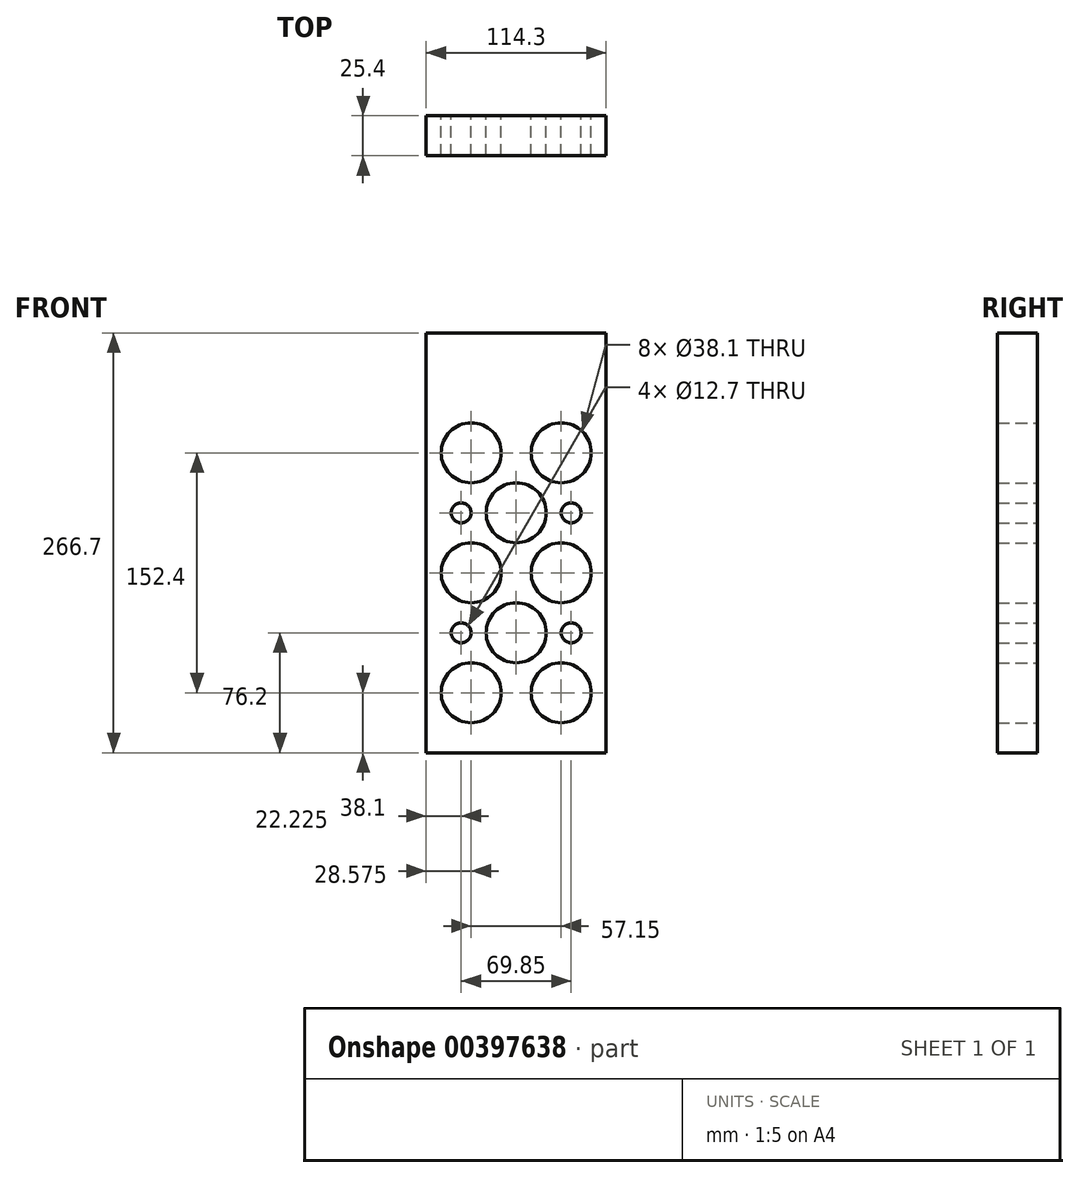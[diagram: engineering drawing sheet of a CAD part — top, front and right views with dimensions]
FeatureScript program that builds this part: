
annotation { "Feature Type Name" : "Feature", "Feature Type Description" : "" }
export const myFeature = defineFeature(function(context is Context, id is Id, definition is map)
    precondition{}
    {
        {
            var Q0;
            Q0=qCreatedBy(makeId("Front.planeOp"),FACE);
            var sketch = newSketch(context, id + "F0", { "sketchPlane" : qUnion([Q0])});
            skLineSegment(sketch, "E0.bottom", {"start": v(0, 0) * mm, "end": v(-114.3, 0) * mm});
            skLineSegment(sketch, "E0.top", {"start": v(0, 266.7) * mm, "end": v(-114.3, 266.7) * mm});
            skLineSegment(sketch, "E0.left", {"start": v(0, 0) * mm, "end": v(0, 266.7) * mm});
            skLineSegment(sketch, "E0.right", {"start": v(-114.3, 0) * mm, "end": v(-114.3, 266.7) * mm});
            skSolve(sketch);
        }
        {
            var Q0;
            Q0=makeQuery(id+"F0.imprint","IMPRINT",FACE,{"disambiguationData":[TD([[makeQuery(id+"F0.imprint","IMPRINT",EDGE,{"derivedFrom":sQuery(id+"F0.wireOp",EDGE,"E0.bottom")}),-1.0]])]});
            var sketch = newSketch(context, id + "F1", { "sketchPlane" : qUnion([Q0])});
            skLineSegment(sketch, "E1", {"start": v(0, 0) * mm, "end": v(-57.15, 0) * mm});
            skLineSegment(sketch, "E2", {"start": v(0, 0) * mm, "end": v(-28.58, 0) * mm});
            skLineSegment(sketch, "E3", {"start": v(0, 0) * mm, "end": v(-85.73, 0) * mm});
            skLineSegment(sketch, "E4", {"start": v(0, 0) * mm, "end": v(-114.3, 0) * mm});
            skLineSegment(sketch, "E5", {"start": v(-28.58, 0) * mm, "end": v(-28.58, 38.1) * mm, "construction": true});
            skLineSegment(sketch, "E6", {"start": v(-85.73, 0) * mm, "end": v(-85.73, 38.1) * mm, "construction": true});
            skCircle(sketch, "E7", {"center": v(-85.73, 38.1) * mm, "radius": 19.05 * mm});
            skCircle(sketch, "E8", {"center": v(-28.58, 38.1) * mm, "radius": 19.05 * mm});
            skLineSegment(sketch, "E9", {"start": v(-57.15, 0) * mm, "end": v(-57.15, 76.2) * mm, "construction": true});
            skCircle(sketch, "E10", {"center": v(-57.15, 76.2) * mm, "radius": 19.05 * mm});
            skCircle(sketch, "E11.0.1.0", {"center": v(-57.15, 152.4) * mm, "radius": 19.05 * mm});
            skCircle(sketch, "E11.0.1.1", {"center": v(-28.58, 114.3) * mm, "radius": 19.05 * mm});
            skCircle(sketch, "E11.0.1.2", {"center": v(-85.73, 114.3) * mm, "radius": 19.05 * mm});
            skCircle(sketch, "E11.0.2.1", {"center": v(-28.58, 190.5) * mm, "radius": 19.05 * mm});
            skCircle(sketch, "E11.0.2.2", {"center": v(-85.73, 190.5) * mm, "radius": 19.05 * mm});
            skLineSegment(sketch, "E11.direction1", {"start": v(-84.46, 31.75) * mm, "end": v(-59.06, 31.75) * mm, "construction": true});
            skLineSegment(sketch, "E11.direction2", {"start": v(-84.46, 31.75) * mm, "end": v(-84.46, 107.95) * mm, "construction": true});
            skSolve(sketch);
        }
        {
            var Q0;
            Q0=makeQuery(id+"F0.imprint","IMPRINT",FACE,{"disambiguationData":[TD([[makeQuery(id+"F0.imprint","IMPRINT",EDGE,{"derivedFrom":sQuery(id+"F0.wireOp",EDGE,"E0.bottom")}),-1.0]])]});
            var sketch = newSketch(context, id + "F2", { "sketchPlane" : qUnion([Q0])});
            skLineSegment(sketch, "E12", {"start": v(0, 0) * mm, "end": v(-22.23, 0) * mm});
            skLineSegment(sketch, "E13", {"start": v(0, 0) * mm, "end": v(-92.08, 0) * mm});
            skPoint(sketch, "E13.endSnap0", {"position": v(-11.11, 0) * mm});
            skLineSegment(sketch, "E14", {"start": v(-22.23, 0) * mm, "end": v(-22.23, 76.2) * mm});
            skLineSegment(sketch, "E15", {"start": v(-92.08, 0) * mm, "end": v(-92.08, 76.2) * mm});
            skCircle(sketch, "E16", {"center": v(-22.23, 76.2) * mm, "radius": 6.35 * mm});
            skCircle(sketch, "E17", {"center": v(-92.08, 76.2) * mm, "radius": 6.35 * mm});
            skCircle(sketch, "E18.0.1.0", {"center": v(-92.08, 152.4) * mm, "radius": 6.35 * mm});
            skCircle(sketch, "E18.0.1.1", {"center": v(-22.23, 152.4) * mm, "radius": 6.35 * mm});
            skLineSegment(sketch, "E18.direction1", {"start": v(-92.08, 76.2) * mm, "end": v(-66.68, 76.2) * mm, "construction": true});
            skLineSegment(sketch, "E18.direction2", {"start": v(-92.08, 76.2) * mm, "end": v(-92.08, 152.4) * mm, "construction": true});
            skSolve(sketch);
        }
        {
            var Q0;
            Q0 = qSketchRegion(id + "F0", true);
            extrude(context, id + "F3", {"entities" : qUnion([Q0]), "depth" : 25.4 * mm});
        }
        {
            var Q0;
            Q0 = qSketchRegion(id + "F1", true);
            extrude(context, id + "F4", {"entities" : qUnion([Q0]), "operationType" : NewBodyOperationType.REMOVE, "depth" : 25.4 * mm});
        }
        {
            var Q0;
            Q0 = qSketchRegion(id + "F2", true);
            extrude(context, id + "F5", {"entities" : qUnion([Q0]), "operationType" : NewBodyOperationType.REMOVE, "depth" : 25.4 * mm});
        }
    });
